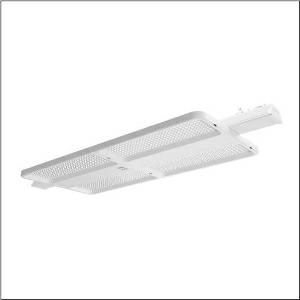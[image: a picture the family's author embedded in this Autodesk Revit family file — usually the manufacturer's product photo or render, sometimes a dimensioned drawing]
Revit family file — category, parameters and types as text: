
# Revit family: highbay_21_fur_licross_r__tragschiene_maxi_52hn11db4qla01_9383
name_source: partatom
category: Lighting Fixtures
units: mm (PartAtom-declared; Revit-internal decimal feet)

## family parameters
Cut with Voids When Loaded = No
Host = Face
Light Source = No
Part Type = Normal
Room Calculation Point = No
Round Connector Dimension = Use Diameter
Shared = No

## types (1)
- --- (1 x LED, 38000 lm, 198.2 W, 4000K)
    Apparent Load = 198 VA
    CIE Flux Codes = 89 97 99 100 100
    Color Rendering = 80
    Color Temperature = 4000K
    Default Elevation = 1800 mm
    Description = high bay luminaire Highbay 21 for Licross® trunking rail maxi; direct symmetric narrow distribution, light control with lens of PMMA; UGR ≤ 19 (X = 4H | Y = 8H | S = 0.25H | reflection values 70/50/20); luminous flux: 38.000lm; light colour: 840, colour temperature: 4000K, MacAdam ≤ 3 SDCM (initial), colour rendering: CRI > 80; luminous efficacy: 191,7lm/W; rated service life: 75.000h (L80/B50) at AT= ta max; control: Bluetooth® Mesh; for wireless networking: Node multi-sensor luminaire for setting up a local control solution without a higher-level application controller, intelligence completely integrated into the luminaire; with auto-swarm function: leading lighting creates safety. The function is already active without any „out-of-the-box“ commissioning; commissioning is not necessary thanks to „out-of-the-box“ functions: basic functions (presence lighting, follow-up times, fading times, etc.) are already preset at the factory; no control line such as DALI between the Node multi-sensor luminaires and Nodes is required, wireless integration of other Node luminaires and Node multi-sensor luminaires into the network is possible; number of Node multi-sensor luminaires in the project can be expanded as required, network sizes > 300 Nodes can be realized; can also be connected to lighting or building automation via various gateways upon request; integrated DALI2 ECG provides luminaire data (according to IEC62386, Part 251), energy data (Part 252), and monitoring and analytics data (Part 253) to higher-level systems for further processing; luminaire with PIR sensor (passive-infrared); with light sensor; luminaire connection: plug, 5-pole, with phase selectionmains connection: 230..240V, AC 50/60Hz; connected load: 198,2W; protection rating (complete): IP64; insulation class (complete): insulation class I (protective earthing); protection symbol: D; certification: CE, ENEC, VDE, UKCA; internal wiring halogen-free; luminaire corresponds to IFS (International Featured Standards) requirements for safety and quality in the food industry; LABS conformity tested according to VDMA 24364:2018-05; housing frame of high-performance plastic PA6, matt traffic white (RAL 9016); cover of PMMA; fixing on rail side of steel, galvanised, white; blank cover of PC/ABS, traffic white (RAL 9016); dimension (LxWxH): 1.250 x 442 x 71mm; permissible operating ambient temperature: -20..+40°C (reducing of maximum allowable ambient temperature of 5°C with ceiling mounting); packaging unit: 1 piece
    Height = 72 mm  [stored 0.23622 ft]
    Lamp = 1 x LED
    Lamp Light Flux = 38000 lm
    Lamp Power = 198.2 W
    Lamp count = 1
    Length = 946 mm
    Luminous efficacy = 192 lm/W
    Manufacturer = Siteco
    ModVariant = No
    Model = 52HN11DB4QLA01
    Mounting Place = Ceiling
    Mounting Type = Pendant
    Number of Poles = 1
    OnlyDefault = Yes
    Power Factor = 1
    Product Name = Highbay 21 für Licross® Tragschiene maxi
    Product group = high bay luminaire
    ProductGroupID = 901
    Protection Class = Protection class I
    Protection Degree = IP 64
    RLX_Detail_Level = 1
    RLX_Emergency_Light_Flux = 0 lm
    RLX_Emergency_Type = 0
    RLX_Emergency_Type_DB = No
    RlxData = <blob elided: 131053 chars, md5=a07015d5>
    Socket = socket
    Standby Power = 0 W
    System Light Flux = 38001 lm
    System Power = 198 W
    Type Comments = factory setting: luminous flux: 100 % | dim-lin: 254 | 918 mA
    Type Image = l_1363271.jpg
    URL = http://relux.com
    VarID = @adj_009771
    Voltage = 0 V
    Weight = 0.00 kg
    Width = 442 mm

note: [stored X ft] marks values corroborated as IEEE doubles in the binary element streams (Revit-internal decimal feet)

## geometry (parser evidence)
native form markers: Blend x4, Sweep x10
no freeform markers — native parametric forms only
